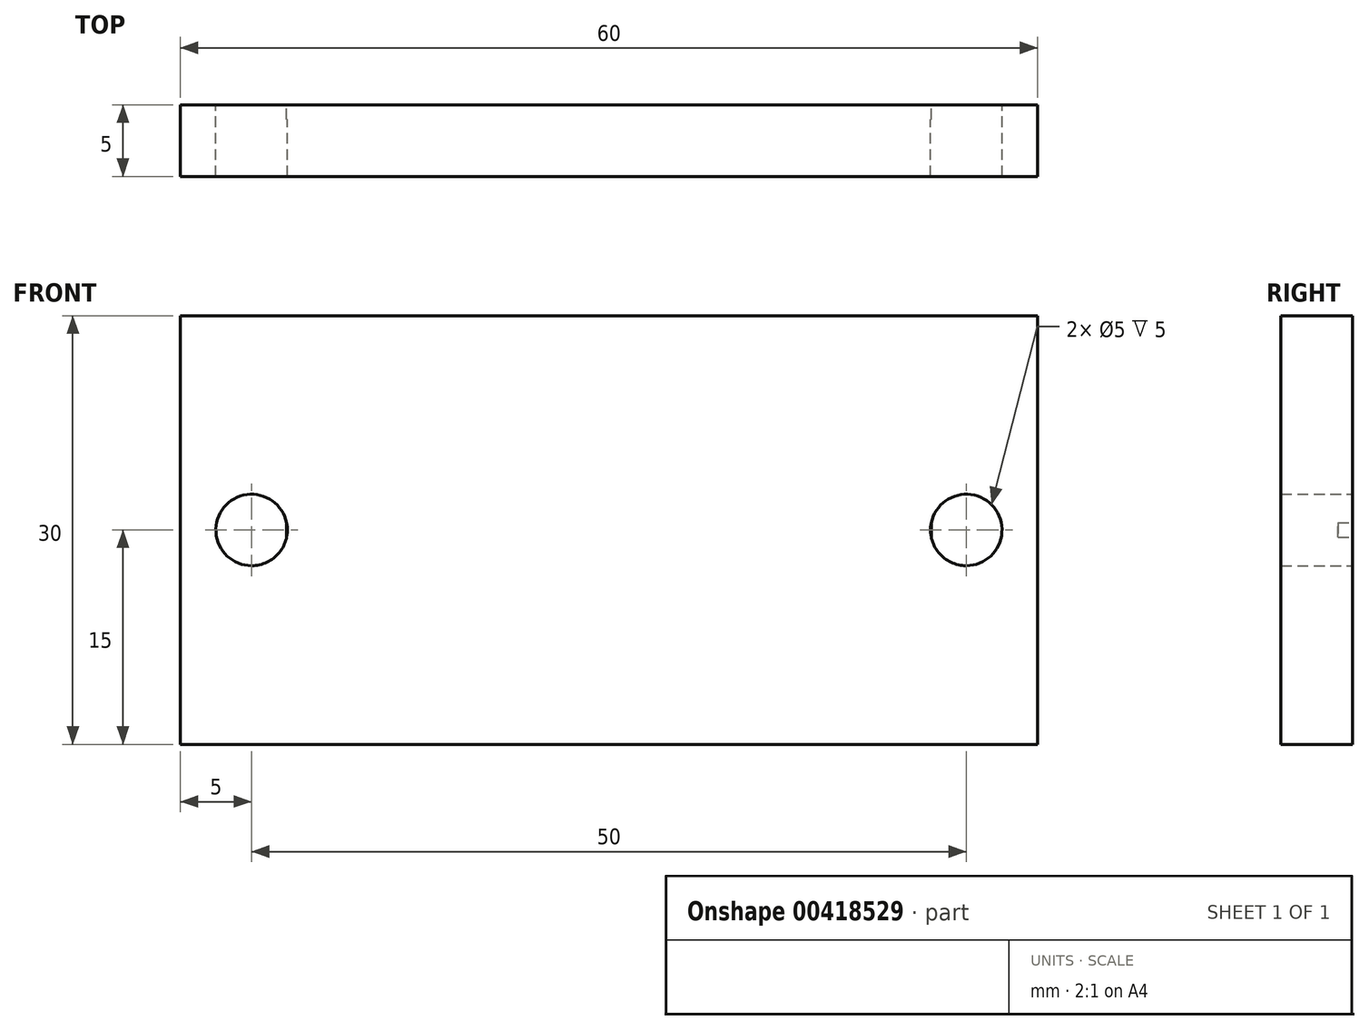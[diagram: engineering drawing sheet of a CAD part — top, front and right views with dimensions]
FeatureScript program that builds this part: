
annotation { "Feature Type Name" : "Feature", "Feature Type Description" : "" }
export const myFeature = defineFeature(function(context is Context, id is Id, definition is map)
    precondition{}
    {
        {
            var Q0;
            Q0=qCreatedBy(makeId("Front.planeOp"),FACE);
            var sketch = newSketch(context, id + "F0", { "sketchPlane" : qUnion([Q0])});
            skLineSegment(sketch, "E0.bottom", {"start": v(-30, 15) * mm, "end": v(30, 15) * mm});
            skLineSegment(sketch, "E0.top", {"start": v(-30, -15) * mm, "end": v(30, -15) * mm});
            skLineSegment(sketch, "E0.left", {"start": v(-30, 15) * mm, "end": v(-30, -15) * mm});
            skLineSegment(sketch, "E0.right", {"start": v(30, 15) * mm, "end": v(30, -15) * mm});
            skPoint(sketch, "E0.middle", {"position": v(0, 0) * mm});
            skCircle(sketch, "E1", {"center": v(25, 0) * mm, "radius": 2.5 * mm});
            skCircle(sketch, "E2", {"center": v(-25, 0) * mm, "radius": 2.5 * mm});
            skSolve(sketch);
        }
        {
            var Q0;
            Q0=makeQuery(id+"F0.imprint","IMPRINT",FACE,{"disambiguationData":[TD([[makeQuery(id+"F0.imprint","IMPRINT",EDGE,{"derivedFrom":sQuery(id+"F0.wireOp",EDGE,"E0.bottom")}),-1.0]])]});
            extrude(context, id + "F1", {"entities" : qUnion([Q0]), "depth" : 5 * mm});
        }
        {
            var Q0;
            Q0=qCreatedBy(makeId("Front.planeOp"),FACE);
            var sketch = newSketch(context, id + "F2", { "sketchPlane" : qUnion([Q0])});
            skLineSegment(sketch, "E3.bottom", {"start": v(22.55, -0.5) * mm, "end": v(-22.55, -0.5) * mm});
            skLineSegment(sketch, "E3.top", {"start": v(22.55, 0.5) * mm, "end": v(-22.55, 0.5) * mm});
            skLineSegment(sketch, "E3.left", {"start": v(22.55, -0.5) * mm, "end": v(22.55, 0.5) * mm});
            skLineSegment(sketch, "E3.right", {"start": v(-22.55, -0.5) * mm, "end": v(-22.55, 0.5) * mm});
            skPoint(sketch, "E3.middle", {"position": v(0, 0) * mm});
            skSolve(sketch);
        }
        {
            var Q0;
            Q0=makeQuery(id+"F2.imprint","IMPRINT",FACE,{"disambiguationData":[TD([[makeQuery(id+"F2.imprint","IMPRINT",EDGE,{"derivedFrom":sQuery(id+"F2.wireOp",EDGE,"E3.bottom")}),-1.0]])]});
            extrude(context, id + "F3", {"entities" : qUnion([Q0]), "operationType" : NewBodyOperationType.ADD, "depth" : 1 * mm});
        }
    });
